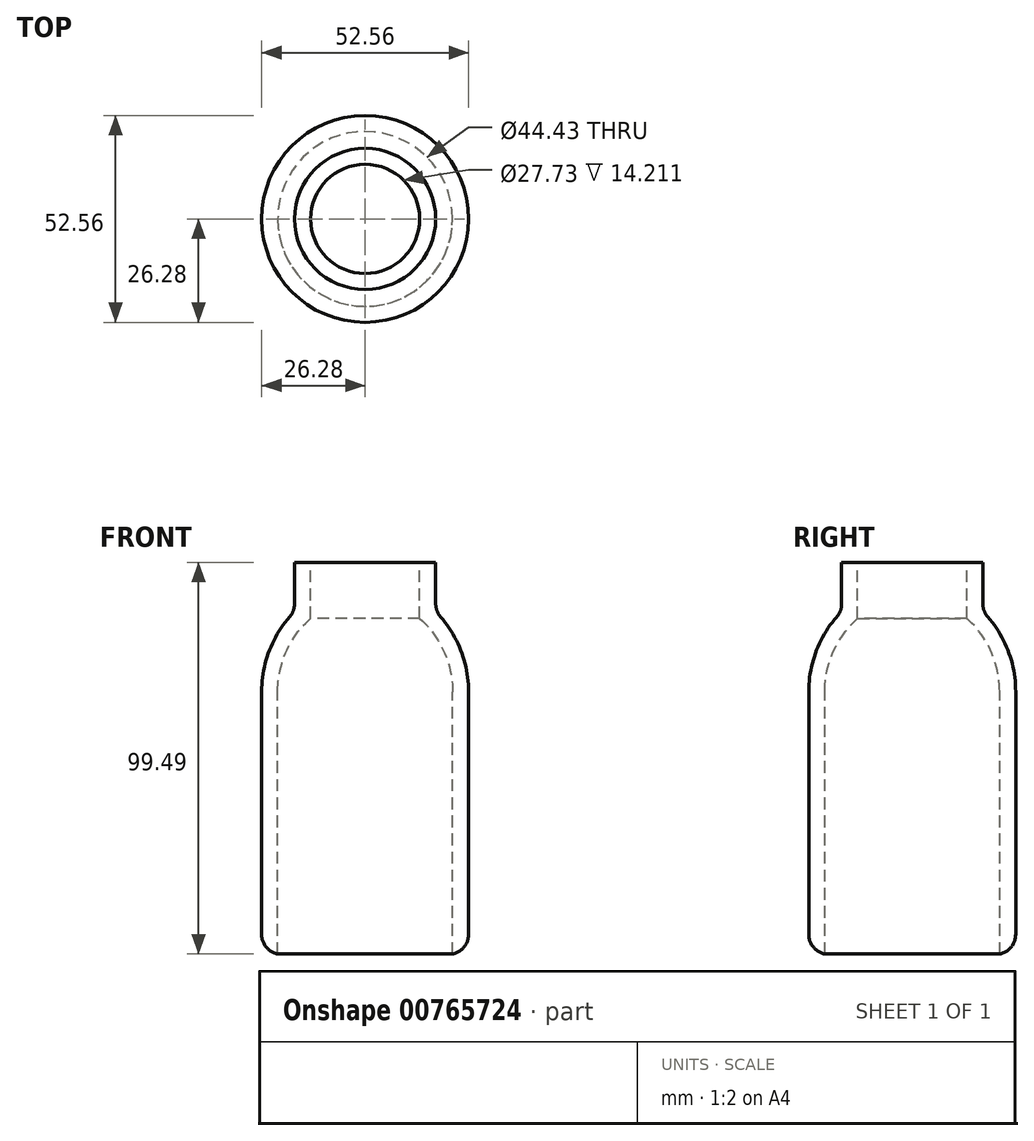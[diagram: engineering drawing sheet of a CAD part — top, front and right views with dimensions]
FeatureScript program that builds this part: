
annotation { "Feature Type Name" : "Feature", "Feature Type Description" : "" }
export const myFeature = defineFeature(function(context is Context, id is Id, definition is map)
    precondition{}
    {
        {
            var Q0;
            Q0=qCreatedBy(makeId("Front.planeOp"),FACE);
            var sketch = newSketch(context, id + "F0", { "sketchPlane" : qUnion([Q0])});
            skLineSegment(sketch, "E0", {"start": v(-22.22, 0) * mm, "end": v(-26.28, 0) * mm});
            skLineSegment(sketch, "E1", {"start": v(-26.28, 0) * mm, "end": v(-26.28, 66.64) * mm});
            skArc(sketch, "E2", {"start": v(-17.93, 87.01) * mm, "mid": v(-24.11, 77.65) * mm, "end": v(-26.28, 66.64) * mm});
            skLineSegment(sketch, "E3", {"start": v(-17.93, 87.01) * mm, "end": v(-17.93, 99.49) * mm});
            skLineSegment(sketch, "E4", {"start": v(-17.93, 99.49) * mm, "end": v(-13.87, 99.49) * mm});
            skLineSegment(sketch, "E5", {"start": v(0, 99.49) * mm, "end": v(0, 0) * mm});
            skLineSegment(sketch, "E6.0", {"start": v(-22.22, 0) * mm, "end": v(-22.22, 66.64) * mm});
            skArc(sketch, "E6.1", {"start": v(-13.87, 85.28) * mm, "mid": v(-20.03, 76.85) * mm, "end": v(-22.22, 66.64) * mm});
            skLineSegment(sketch, "E6.2", {"start": v(-13.87, 85.28) * mm, "end": v(-13.87, 99.49) * mm});
            skSolve(sketch);
        }
        {
            var Q0;
            Q0 = qSketchRegion(id + "F0", true);
            var Q1;
            Q1=sQuery(id+"F0.wireOp",EDGE,"E5");
            revolve(context, id + "F1", {"surfaceOperationType" : NewSurfaceOperationType.NEW, "entities" : qUnion([Q0]), "axis" : qUnion([Q1]), "revolveType" : RevolveType.FULL});
        }
        {
            var Q0;
            Q0=makeQuery(id+"F1.opRevolve","SWEPT_EDGE",EDGE,{"disambiguationData":[OSD([sQuery(id+"F0.wireOp",EDGE,"E0"),sQuery(id+"F0.wireOp",EDGE,"E1")])]});
            fillet(context, id + "F2", {"entities" : qUnion([Q0]), "radius" : 5.08 * mm, "tangentPropagation" : true, "allowEdgeOverflow" : false});
        }
        {
            var Q0;
            Q0=makeQuery(id+"F1.opRevolve","SWEPT_EDGE",EDGE,{"disambiguationData":[OSD([sQuery(id+"F0.wireOp",EDGE,"E2"),sQuery(id+"F0.wireOp",EDGE,"E3")])]});
            fillet(context, id + "F3", {"entities" : qUnion([Q0]), "radius" : 5.08 * mm, "tangentPropagation" : true, "allowEdgeOverflow" : false});
        }
    });
